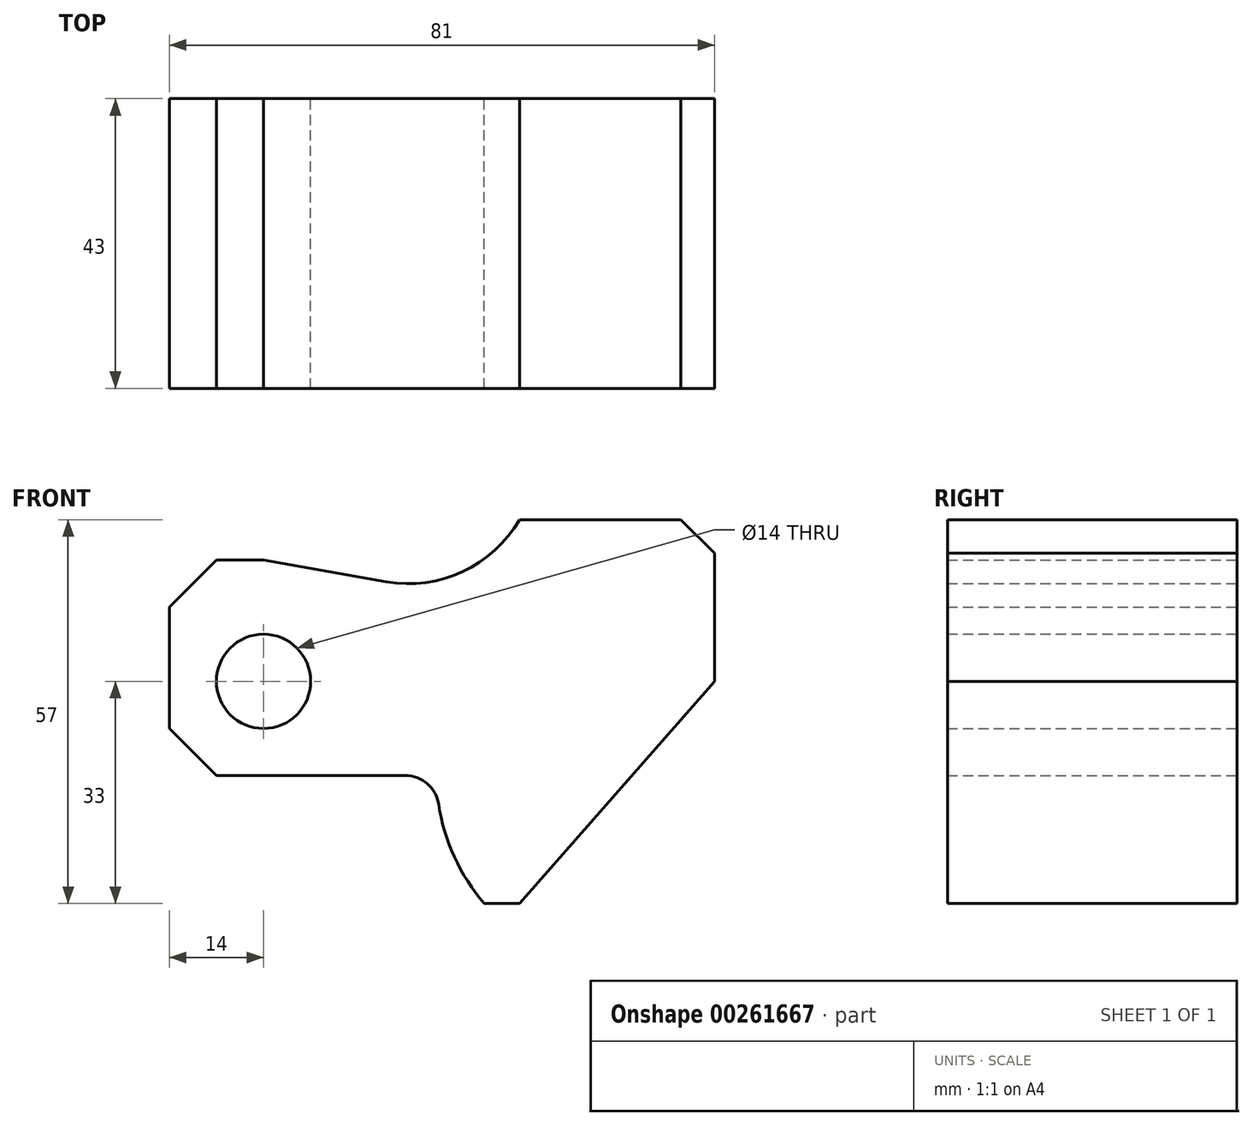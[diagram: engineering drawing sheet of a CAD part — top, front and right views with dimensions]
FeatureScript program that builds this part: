
annotation { "Feature Type Name" : "Feature", "Feature Type Description" : "" }
export const myFeature = defineFeature(function(context is Context, id is Id, definition is map)
    precondition{}
    {
        {
            var Q0;
            Q0=qCreatedBy(makeId("Front.planeOp"),FACE);
            var sketch = newSketch(context, id + "F0", { "sketchPlane" : qUnion([Q0])});
            skLineSegment(sketch, "E0", {"start": v(0, 0) * mm, "end": v(0, 18) * mm});
            skLineSegment(sketch, "E1", {"start": v(0, 18) * mm, "end": v(7, 25) * mm});
            skLineSegment(sketch, "E2", {"start": v(7, 25) * mm, "end": v(14, 25) * mm});
            skLineSegment(sketch, "E3", {"start": v(14, 25) * mm, "end": v(32.24, 21.78) * mm});
            skLineSegment(sketch, "E4", {"start": v(0, 0) * mm, "end": v(7, -7) * mm});
            skLineSegment(sketch, "E5", {"start": v(7, -7) * mm, "end": v(35.07, -7) * mm});
            skCircle(sketch, "E6", {"center": v(14, 7) * mm, "radius": 7 * mm});
            skLineSegment(sketch, "E7", {"start": v(76, 31) * mm, "end": v(81, 26) * mm});
            skLineSegment(sketch, "E8", {"start": v(81, 26) * mm, "end": v(81, 7) * mm});
            skLineSegment(sketch, "E9", {"start": v(81, 7) * mm, "end": v(52, -26) * mm});
            skLineSegment(sketch, "E10", {"start": v(52, -26) * mm, "end": v(46.79, -26) * mm});
            skLineSegment(sketch, "E11", {"start": v(76, 31) * mm, "end": v(52, 31) * mm});
            skLineSegment(sketch, "E12", {"start": v(52, -26) * mm, "end": v(81.78, -26) * mm, "construction": true});
            skLineSegment(sketch, "E13", {"start": v(68.7, -26) * mm, "end": v(68.7, -7) * mm, "construction": true});
            skArc(sketch, "E14", {"start": v(40.01, -11.26) * mm, "mid": v(42.35, -19.12) * mm, "end": v(46.79, -26) * mm});
            skArc(sketch, "E15", {"start": v(40.01, -11.26) * mm, "mid": v(38.33, -8.21) * mm, "end": v(35.07, -7) * mm});
            skArc(sketch, "E16", {"start": v(32.24, 21.78) * mm, "mid": v(43.57, 23.28) * mm, "end": v(52, 31) * mm});
            skSolve(sketch);
        }
        {
            var Q0;
            Q0=makeQuery(id+"F0.imprint","IMPRINT",FACE,{"disambiguationData":[TD([[makeQuery(id+"F0.imprint","IMPRINT",EDGE,{"derivedFrom":sQuery(id+"F0.wireOp",EDGE,"E0")}),-1.0]])]});
            extrude(context, id + "F1", {"entities" : qUnion([Q0]), "depth" : 43 * mm});
        }
    });
